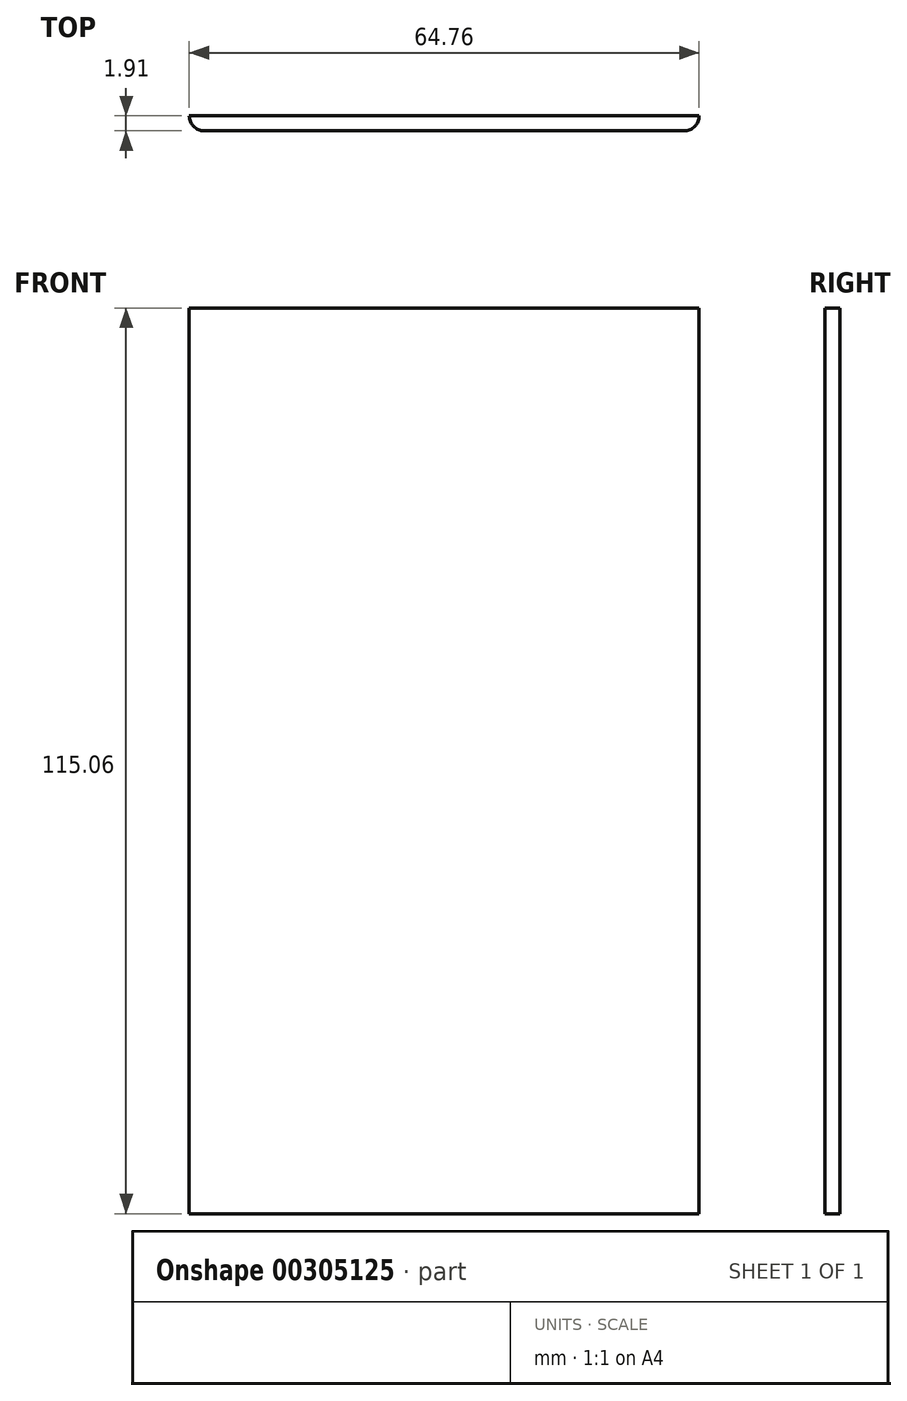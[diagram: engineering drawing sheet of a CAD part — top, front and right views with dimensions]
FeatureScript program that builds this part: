
annotation { "Feature Type Name" : "Feature", "Feature Type Description" : "" }
export const myFeature = defineFeature(function(context is Context, id is Id, definition is map)
    precondition{}
    {
        {
            var Q0;
            Q0=qCreatedBy(makeId("Front.planeOp"),FACE);
            var sketch = newSketch(context, id + "F0", { "sketchPlane" : qUnion([Q0])});
            skLineSegment(sketch, "E0.bottom", {"start": v(32.39, 57.53) * mm, "end": v(-32.39, 57.53) * mm});
            skLineSegment(sketch, "E0.top", {"start": v(32.38, -57.53) * mm, "end": v(-32.39, -57.53) * mm});
            skLineSegment(sketch, "E0.left", {"start": v(32.39, 57.53) * mm, "end": v(32.38, -57.53) * mm});
            skLineSegment(sketch, "E0.right", {"start": v(-32.39, 57.53) * mm, "end": v(-32.39, -57.53) * mm});
            skPoint(sketch, "E0.middle", {"position": v(0, 0) * mm});
            skSolve(sketch);
        }
        {
            var Q0;
            Q0=makeQuery(id+"F0.imprint","IMPRINT",FACE,{"disambiguationData":[TD([[makeQuery(id+"F0.imprint","IMPRINT",EDGE,{"derivedFrom":sQuery(id+"F0.wireOp",EDGE,"E0.bottom")}),1.0]])]});
            extrude(context, id + "F1", {"entities" : qUnion([Q0]), "depth" : 2.54 * mm});
        }
        {
            var Q0;
            Q0=makeQuery(id+"F1.opExtrude","CAP_EDGE",EDGE,{"disambiguationData":[OSD([sQuery(id+"F0.wireOp",EDGE,"E0.left")])],"isStart":false});
            fillet(context, id + "F2", {"entities" : qUnion([Q0]), "radius" : 1.9 * mm, "tangentPropagation" : true, "allowEdgeOverflow" : false});
        }
        {
            var Q0;
            Q0=makeQuery(id+"F1.opExtrude","CAP_EDGE",EDGE,{"disambiguationData":[OSD([sQuery(id+"F0.wireOp",EDGE,"E0.right")])],"isStart":false});
            fillet(context, id + "F3", {"entities" : qUnion([Q0]), "radius" : 1.9 * mm, "tangentPropagation" : true, "allowEdgeOverflow" : false});
        }
        {
            var Q0;
            Q0=makeQuery(id+"F1.opExtrude","CAP_FACE",FACE,{"disambiguationData":[OSD([sQuery(id+"F0.wireOp",EDGE,"E0.bottom"),sQuery(id+"F0.wireOp",EDGE,"E0.top"),sQuery(id+"F0.wireOp",EDGE,"E0.left"),sQuery(id+"F0.wireOp",EDGE,"E0.right")])],"isStart":true});
            extrude(context, id + "F4", {"entities" : qUnion([Q0]), "operationType" : NewBodyOperationType.REMOVE, "oppositeDirection" : true, "depth" : 0.64 * mm});
        }
    });
